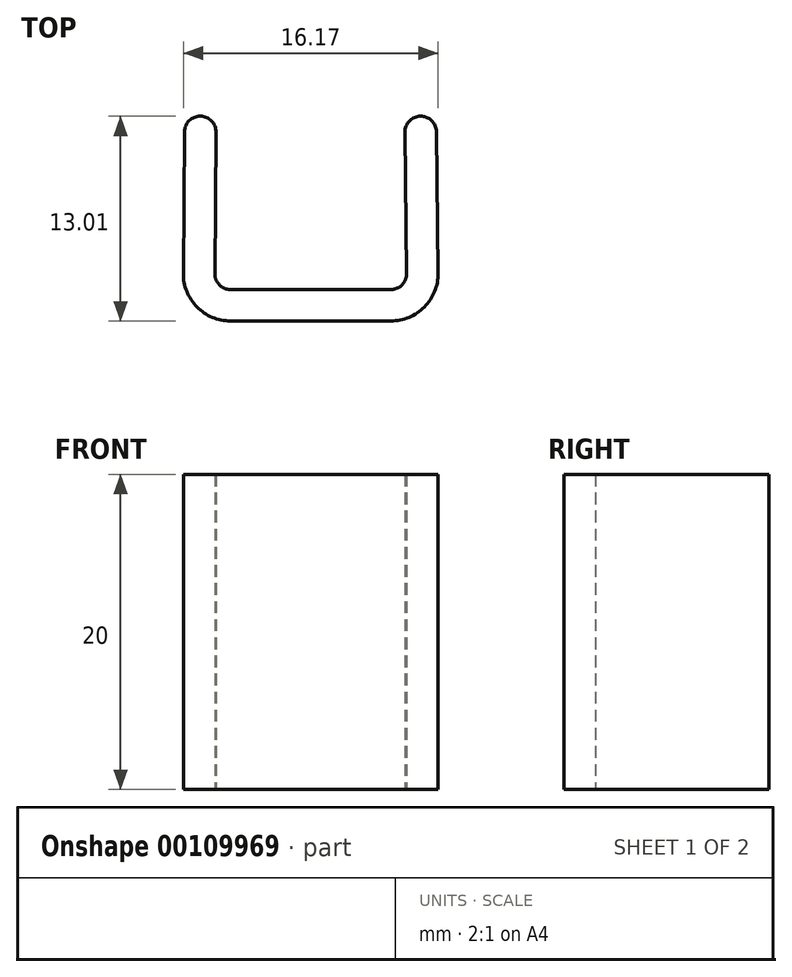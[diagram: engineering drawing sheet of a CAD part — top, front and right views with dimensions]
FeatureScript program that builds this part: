
annotation { "Feature Type Name" : "Feature", "Feature Type Description" : "" }
export const myFeature = defineFeature(function(context is Context, id is Id, definition is map)
    precondition{}
    {
        {
            var Q0;
            Q0=qCreatedBy(makeId("Top.planeOp"),FACE);
            var sketch = newSketch(context, id + "F0", { "sketchPlane" : qUnion([Q0])});
            skLineSegment(sketch, "E0", {"start": v(0.1, 12.02) * mm, "end": v(0.03, 3.02) * mm});
            skLineSegment(sketch, "E1", {"start": v(3.03, 0) * mm, "end": v(13.2, 0) * mm});
            skLineSegment(sketch, "E2", {"start": v(16.2, 3.04) * mm, "end": v(16.1, 12.02) * mm});
            skLineSegment(sketch, "E3", {"start": v(14.1, 12) * mm, "end": v(14.2, 3.01) * mm});
            skLineSegment(sketch, "E4", {"start": v(13.2, 2) * mm, "end": v(3.03, 2) * mm});
            skLineSegment(sketch, "E5", {"start": v(2.03, 3) * mm, "end": v(2.1, 12) * mm});
            skArc(sketch, "E6", {"start": v(2.1, 12) * mm, "mid": v(1.1, 13) * mm, "end": v(0.1, 12.02) * mm});
            skArc(sketch, "E7", {"start": v(16.1, 12.02) * mm, "mid": v(15.09, 13) * mm, "end": v(14.1, 12) * mm});
            skPoint(sketch, "E8.visualSharp", {"position": v(2.02, 2) * mm});
            skArc(sketch, "E8.filletArc", {"start": v(2.03, 3) * mm, "mid": v(2.32, 2.3) * mm, "end": v(3.03, 2) * mm});
            skPoint(sketch, "E9.visualSharp", {"position": v(14.22, 2) * mm});
            skArc(sketch, "E9.filletArc", {"start": v(13.2, 2) * mm, "mid": v(13.92, 2.3) * mm, "end": v(14.2, 3.01) * mm});
            skPoint(sketch, "E10.visualSharp", {"position": v(0, 0) * mm});
            skArc(sketch, "E10.filletArc", {"start": v(0.03, 3.02) * mm, "mid": v(0.9, 0.89) * mm, "end": v(3.03, 0) * mm});
            skPoint(sketch, "E11.visualSharp", {"position": v(16.24, 0) * mm});
            skArc(sketch, "E11.filletArc", {"start": v(13.2, 0) * mm, "mid": v(15.34, 0.9) * mm, "end": v(16.2, 3.04) * mm});
            skSolve(sketch);
        }
        {
            var Q0;
            Q0 = qSketchRegion(id + "F0", true);
            extrude(context, id + "F1", {"entities" : qUnion([Q0]), "depth" : 20 * mm});
        }
    });
